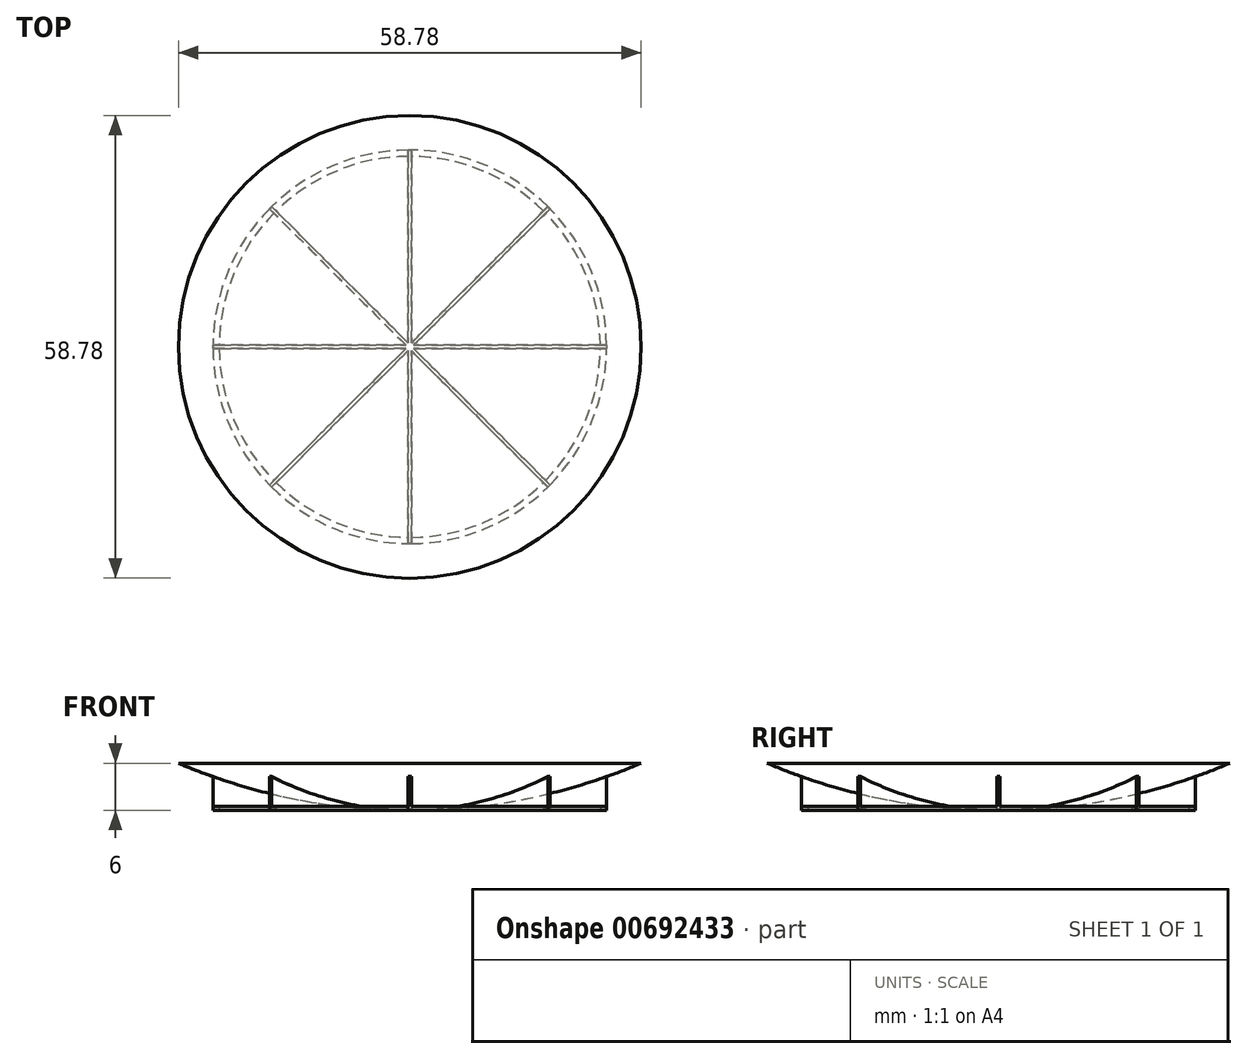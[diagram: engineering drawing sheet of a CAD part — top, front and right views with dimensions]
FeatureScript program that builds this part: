
annotation { "Feature Type Name" : "Feature", "Feature Type Description" : "" }
export const myFeature = defineFeature(function(context is Context, id is Id, definition is map)
    precondition{}
    {
        {
            var Q0;
            Q0=qCreatedBy(makeId("Top.planeOp"),FACE);
            var sketch = newSketch(context, id + "F0", { "sketchPlane" : qUnion([Q0])});
            skCircle(sketch, "E0", {"center": v(0, 0) * mm, "radius": 25 * mm, "construction": true});
            skLineSegment(sketch, "E1.bottom", {"start": v(-25, 0.2) * mm, "end": v(0, 0.2) * mm});
            skLineSegment(sketch, "E1.top", {"start": v(-25, -0.2) * mm, "end": v(0, -0.2) * mm});
            skLineSegment(sketch, "E1.left", {"start": v(-25, 0.2) * mm, "end": v(-25, -0.2) * mm});
            skLineSegment(sketch, "E1.right", {"start": v(0, 0.2) * mm, "end": v(0, -0.2) * mm});
            skLineSegment(sketch, "E2", {"start": v(0, 0) * mm, "end": v(-25, 0) * mm, "construction": true});
            skSolve(sketch);
        }
        {
            var Q0;
            Q0 = qSketchRegion(id + "F0", true);
            extrude(context, id + "F1", {"entities" : qUnion([Q0]), "depth" : 5 * mm, "offsetDistance" : 25 * mm});
        }
        {
            var Q0;
            Q0=qCreatedBy(makeId("Front.planeOp"),FACE);
            var sketch = newSketch(context, id + "F2", { "sketchPlane" : qUnion([Q0])});
            skLineSegment(sketch, "E3", {"start": v(0, 0) * mm, "end": v(0, 13.35) * mm});
            skSolve(sketch);
        }
        {
            var Q0;
            Q0=makeQuery(id+"F1.opExtrude","SWEPT_BODY",BODY,{"disambiguationData":[OSD([sQuery(id+"F0.wireOp",EDGE,"E1.bottom"),sQuery(id+"F0.wireOp",EDGE,"E1.top"),sQuery(id+"F0.wireOp",EDGE,"E1.left"),sQuery(id+"F0.wireOp",EDGE,"E1.right")])]});
            var Q1;
            Q1=sQuery(id+"F2.wireOp",EDGE,"E3");
            circularPattern(context, id + "F3", {"operationType" : NewBodyOperationType.ADD, "entities" : qUnion([Q0]), "axis" : qUnion([Q1]), "angle" : 360 * degree, "instanceCount" : 8, "equalSpace" : true});
        }
        {
            var Q0;
            Q0=qCreatedBy(makeId("Front.planeOp"),FACE);
            var sketch = newSketch(context, id + "F4", { "sketchPlane" : qUnion([Q0])});
            skArc(sketch, "E4", {"start": v(-29.4, 6) * mm, "mid": v(-15, 1.52) * mm, "end": v(0, 0) * mm});
            skLineSegment(sketch, "E5", {"start": v(0, 0) * mm, "end": v(0, 6) * mm});
            skLineSegment(sketch, "E6", {"start": v(0, 6) * mm, "end": v(-29.4, 6) * mm});
            skSolve(sketch);
        }
        {
            var Q0;
            Q0 = qSketchRegion(id + "F4", true);
            var Q1;
            Q1=sQuery(id+"F2.wireOp",EDGE,"E3");
            revolve(context, id + "F5", {"operationType" : NewBodyOperationType.ADD, "entities" : qUnion([Q0]), "axis" : qUnion([Q1]), "revolveType" : RevolveType.FULL});
        }
        {
            var Q0;
            Q0=qCreatedBy(makeId("Top.planeOp"),FACE);
            var sketch = newSketch(context, id + "F6", { "sketchPlane" : qUnion([Q0])});
            skCircle(sketch, "E7.0", {"center": v(0, 0) * mm, "radius": 25 * mm});
            skLineSegment(sketch, "E7.1", {"start": v(-25, 0.2) * mm, "end": v(0, 0.2) * mm});
            skLineSegment(sketch, "E7.2", {"start": v(-25, -0.2) * mm, "end": v(0, -0.2) * mm});
            skLineSegment(sketch, "E7.3", {"start": v(-25, 0.2) * mm, "end": v(-25, -0.2) * mm});
            skLineSegment(sketch, "E7.4", {"start": v(0, 0.2) * mm, "end": v(0, -0.2) * mm});
            skLineSegment(sketch, "E7.5", {"start": v(0, 0) * mm, "end": v(-25, 0) * mm});
            skCircle(sketch, "E8", {"center": v(0, 0) * mm, "radius": 24.2 * mm});
            skSolve(sketch);
        }
        {
            var Q0;
            Q0 = qSketchRegion(id + "F6", true);
            extrude(context, id + "F7", {"entities" : qUnion([Q0]), "operationType" : NewBodyOperationType.ADD, "depth" : 0.5 * mm, "offsetDistance" : 25 * mm});
        }
    });
